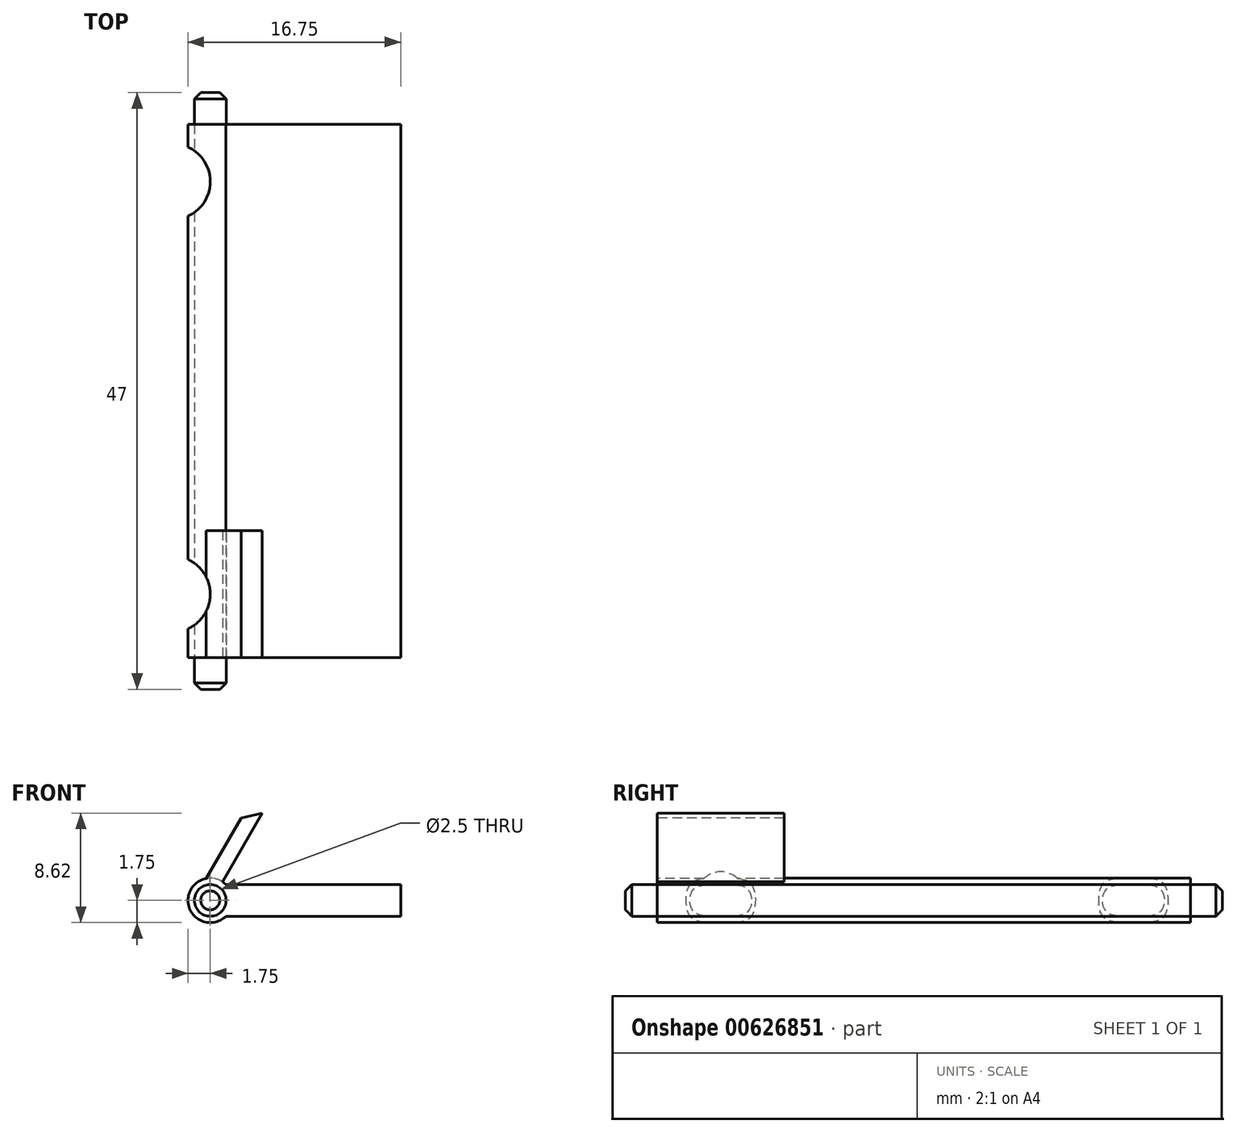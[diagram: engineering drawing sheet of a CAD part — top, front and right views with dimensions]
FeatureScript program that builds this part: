
annotation { "Feature Type Name" : "Feature", "Feature Type Description" : "" }
export const myFeature = defineFeature(function(context is Context, id is Id, definition is map)
    precondition{}
    {
        {
            var Q0;
            Q0=qCreatedBy(makeId("Front.planeOp"),FACE);
            var sketch = newSketch(context, id + "F0", { "sketchPlane" : qUnion([Q0])});
            skCircle(sketch, "E0", {"center": v(0, 0) * mm, "radius": 1.75 * mm});
            skLineSegment(sketch, "E1.bottom", {"start": v(1.22, -1.25) * mm, "end": v(15, -1.25) * mm});
            skLineSegment(sketch, "E1.top", {"start": v(1.22, 1.25) * mm, "end": v(15, 1.25) * mm});
            skLineSegment(sketch, "E1.left", {"start": v(1.22, 1.25) * mm, "end": v(1.22, -1.25) * mm});
            skLineSegment(sketch, "E1.right", {"start": v(15, 1.25) * mm, "end": v(15, -1.25) * mm});
            skLineSegment(sketch, "E2", {"start": v(0.84, 1.25) * mm, "end": v(0.96, 1.46) * mm});
            skLineSegment(sketch, "E3", {"start": v(-0.3, 1.72) * mm, "end": v(2.44, 6.49) * mm});
            skLineSegment(sketch, "E4", {"start": v(4.09, 6.87) * mm, "end": v(2.44, 6.49) * mm});
            skCircle(sketch, "E5", {"center": v(0, 0) * mm, "radius": 1.25 * mm});
            skLineSegment(sketch, "E6.trimOffspring", {"start": v(0.84, 1.25) * mm, "end": v(4.09, 6.87) * mm});
            skSolve(sketch);
        }
        {
            var Q0;
            Q0=makeQuery(id+"F0.imprint","IMPRINT",FACE,{"disambiguationData":[TD([[makeQuery(id+"F0.imprint","IMPRINT",EDGE,{"derivedFrom":sQuery(id+"F0.wireOp",EDGE,"E5")}),1.0]])]});
            extrude(context, id + "F1", {"entities" : qUnion([Q0]), "depth" : 2.5 * mm, "offsetDistance" : 25 * mm});
        }
        {
            var Q0;
            Q0=makeQuery(id+"F1.opExtrude","CAP_EDGE",EDGE,{"disambiguationData":[OSD([sQuery(id+"F0.wireOp",EDGE,"E5")])],"isStart":false});
            chamfer(context, id + "F2", {"entities" : qUnion([Q0]), "width" : 0.5 * mm, "tangentPropagation" : true});
        }
        {
            var Q0;
            {var subQ1=sQuery(id+"F0.wireOp",EDGE,"E1.bottom");Q0=makeQuery(id+"F0.imprint","IMPRINT",FACE,{"disambiguationData":[TD([[makeQuery(id+"F0.imprint","IMPRINT",EDGE,{"derivedFrom":subQ1}),1.0]])]});}
            var Q1;
            {var subQ0=sQuery(id+"F0.wireOp",EDGE,"E1.left");Q1=makeQuery(id+"F0.imprint","IMPRINT",FACE,{"disambiguationData":[TD([[makeQuery(id+"F0.imprint","IMPRINT",EDGE,{"derivedFrom":subQ0}),-1.0]])]});}
            var Q2;
            {var subQ0=sQuery(id+"F0.wireOp",EDGE,"E1.left");Q2=makeQuery(id+"F0.imprint","IMPRINT",FACE,{"disambiguationData":[TD([[makeQuery(id+"F0.imprint","IMPRINT",EDGE,{"derivedFrom":subQ0}),1.0]])]});}
            extrude(context, id + "F3", {"entities" : qUnion([Q0, Q1, Q2]), "operationType" : NewBodyOperationType.ADD, "oppositeDirection" : true, "depth" : 42 * mm, "offsetDistance" : 25 * mm});
        }
        {
            var Q0;
            Q0=makeQuery(id+"F0.imprint","IMPRINT",FACE,{"disambiguationData":[TD([[makeQuery(id+"F0.imprint","IMPRINT",EDGE,{"derivedFrom":sQuery(id+"F0.wireOp",EDGE,"E5")}),1.0]])]});
            extrude(context, id + "F4", {"entities" : qUnion([Q0]), "oppositeDirection" : true, "depth" : 44.5 * mm, "offsetDistance" : 25 * mm});
        }
        {
            var Q0;
            Q0=makeQuery(id+"F4.opExtrude","CAP_EDGE",EDGE,{"disambiguationData":[OSD([sQuery(id+"F0.wireOp",EDGE,"E5")])],"isStart":false});
            chamfer(context, id + "F5", {"entities" : qUnion([Q0]), "width" : 0.5 * mm, "tangentPropagation" : true});
        }
        {
            var Q0;
            Q0=makeQuery(id+"F3.opExtrude","SWEPT_FACE",FACE,{"disambiguationData":[OSD([sQuery(id+"F0.wireOp",EDGE,"E1.top")])]});
            var sketch = newSketch(context, id + "F6", { "sketchPlane" : qUnion([Q0])});
            skCircle(sketch, "E7", {"center": v(-3, 5) * mm, "radius": 3 * mm});
            skCircle(sketch, "E8", {"center": v(-3, 37.5) * mm, "radius": 3 * mm});
            skSolve(sketch);
        }
        {
            var Q0;
            {var subQ0=sQuery(id+"F0.wireOp",EDGE,"E3");Q0=makeQuery(id+"F0.imprint","IMPRINT",FACE,{"disambiguationData":[TD([[makeQuery(id+"F0.imprint","IMPRINT",EDGE,{"derivedFrom":subQ0}),-1.0]])]});}
            extrude(context, id + "F7", {"entities" : qUnion([Q0]), "operationType" : NewBodyOperationType.ADD, "oppositeDirection" : true, "depth" : 10 * mm, "offsetDistance" : 25 * mm});
        }
        {
            var Q0;
            Q0=makeQuery(id+"F6.imprint","IMPRINT",FACE,{"disambiguationData":[TD([[makeQuery(id+"F6.imprint","IMPRINT",EDGE,{"derivedFrom":sQuery(id+"F6.wireOp",EDGE,"E8")}),1.0]])]});
            var Q1;
            Q1=makeQuery(id+"F6.imprint","IMPRINT",FACE,{"disambiguationData":[TD([[makeQuery(id+"F6.imprint","IMPRINT",EDGE,{"derivedFrom":sQuery(id+"F6.wireOp",EDGE,"E7")}),1.0]])]});
            extrude(context, id + "F8", {"entities" : qUnion([Q0, Q1]), "operationType" : NewBodyOperationType.REMOVE, "oppositeDirection" : true, "depth" : 10 * mm, "offsetDistance" : 25 * mm, "hasSecondDirection" : true, "secondDirectionOppositeDirection" : false, "secondDirectionDepth" : 10 * mm});
        }
    });
